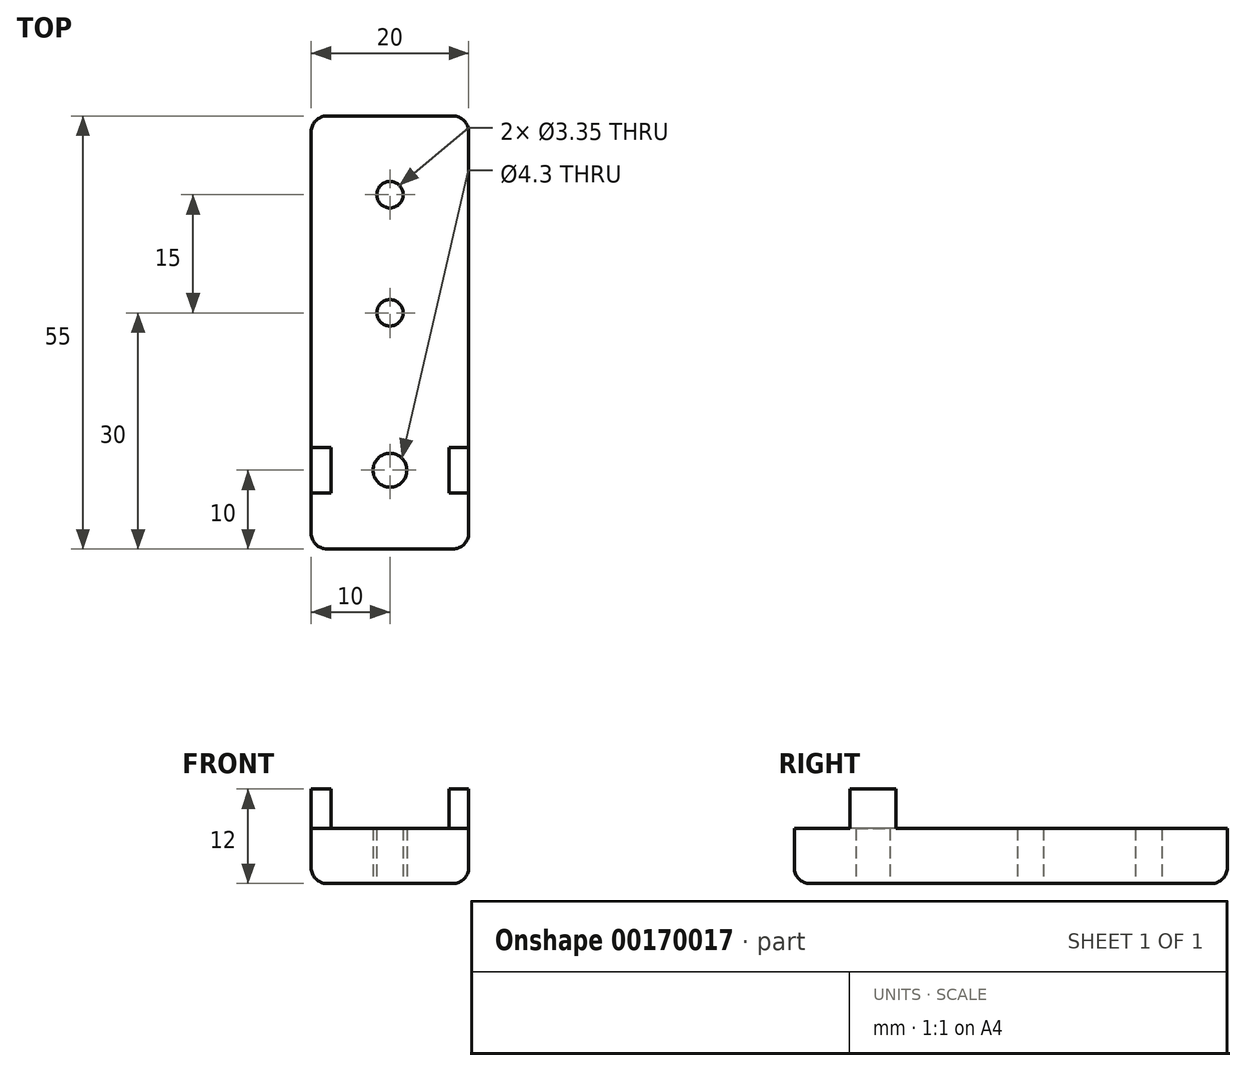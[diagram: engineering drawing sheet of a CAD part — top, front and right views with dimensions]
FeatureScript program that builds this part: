
annotation { "Feature Type Name" : "Feature", "Feature Type Description" : "" }
export const myFeature = defineFeature(function(context is Context, id is Id, definition is map)
    precondition{}
    {
        {
            var Q0;
            Q0=qCreatedBy(makeId("Top.planeOp"),FACE);
            var sketch = newSketch(context, id + "F0", { "sketchPlane" : qUnion([Q0])});
            skLineSegment(sketch, "E0.bottom", {"start": v(-10, 0) * mm, "end": v(10, 0) * mm});
            skLineSegment(sketch, "E0.top", {"start": v(-10, 55) * mm, "end": v(10, 55) * mm});
            skLineSegment(sketch, "E0.left", {"start": v(-10, 0) * mm, "end": v(-10, 55) * mm});
            skLineSegment(sketch, "E0.right", {"start": v(10, 0) * mm, "end": v(10, 55) * mm});
            skLineSegment(sketch, "E1.bottom", {"start": v(-7.5, 7.1) * mm, "end": v(-10, 7.1) * mm});
            skLineSegment(sketch, "E1.top", {"start": v(-7.5, 12.9) * mm, "end": v(-10, 12.9) * mm});
            skLineSegment(sketch, "E1.left", {"start": v(-7.5, 7.1) * mm, "end": v(-7.5, 12.9) * mm});
            skPoint(sketch, "E1.middle", {"position": v(-10, 10) * mm});
            skLineSegment(sketch, "E2.bottom", {"start": v(7.5, 12.9) * mm, "end": v(10, 12.9) * mm});
            skLineSegment(sketch, "E2.top", {"start": v(7.5, 7.1) * mm, "end": v(10, 7.1) * mm});
            skLineSegment(sketch, "E2.left", {"start": v(7.5, 12.9) * mm, "end": v(7.5, 7.1) * mm});
            skPoint(sketch, "E2.middle.positionSnap0", {"position": v(-7.5, 10) * mm});
            skPoint(sketch, "E2.centerSnap0", {"position": v(-7.5, 10) * mm});
            skCircle(sketch, "E3", {"center": v(0, 10) * mm, "radius": 2.15 * mm});
            skCircle(sketch, "E4", {"center": v(0, 45) * mm, "radius": 1.68 * mm});
            skPoint(sketch, "E4.centerSnap0", {"position": v(0, 55) * mm});
            skCircle(sketch, "E5", {"center": v(0, 30) * mm, "radius": 1.68 * mm});
            skSolve(sketch);
        }
        {
            var Q0;
            {var subQ5=sQuery(id+"F0.wireOp",EDGE,"E0.bottom");Q0=makeQuery(id+"F0.imprint","IMPRINT",FACE,{"disambiguationData":[TD([[makeQuery(id+"F0.imprint","IMPRINT",EDGE,{"derivedFrom":subQ5}),1.0]])]});}
            var Q1;
            {var subQ0=sQuery(id+"F0.wireOp",EDGE,"E1.bottom");Q1=makeQuery(id+"F0.imprint","IMPRINT",FACE,{"disambiguationData":[TD([[makeQuery(id+"F0.imprint","IMPRINT",EDGE,{"derivedFrom":subQ0}),-1.0]])]});}
            var Q2;
            {var subQ0=sQuery(id+"F0.wireOp",EDGE,"E2.bottom");Q2=makeQuery(id+"F0.imprint","IMPRINT",FACE,{"disambiguationData":[TD([[makeQuery(id+"F0.imprint","IMPRINT",EDGE,{"derivedFrom":subQ0}),-1.0]])]});}
            extrude(context, id + "F1", {"entities" : qUnion([Q0, Q1, Q2]), "depth" : 7 * mm});
        }
        {
            var Q0;
            {var subQ0=sQuery(id+"F0.wireOp",EDGE,"E1.bottom");Q0=makeQuery(id+"F0.imprint","IMPRINT",FACE,{"disambiguationData":[TD([[makeQuery(id+"F0.imprint","IMPRINT",EDGE,{"derivedFrom":subQ0}),-1.0]])]});}
            var Q1;
            {var subQ0=sQuery(id+"F0.wireOp",EDGE,"E2.bottom");Q1=makeQuery(id+"F0.imprint","IMPRINT",FACE,{"disambiguationData":[TD([[makeQuery(id+"F0.imprint","IMPRINT",EDGE,{"derivedFrom":subQ0}),-1.0]])]});}
            extrude(context, id + "F2", {"entities" : qUnion([Q0, Q1]), "operationType" : NewBodyOperationType.ADD, "depth" : (7 + 5) * mm});
        }
        {
            var Q0;
            Q0=makeQuery(id+"F1.opExtrude","SWEPT_EDGE",EDGE,{"disambiguationData":[OSD([sQuery(id+"F0.wireOp",EDGE,"E0.bottom"),sQuery(id+"F0.wireOp",EDGE,"E0.right")])]});
            var Q1;
            Q1=makeQuery(id+"F1.opExtrude","SWEPT_EDGE",EDGE,{"disambiguationData":[OSD([sQuery(id+"F0.wireOp",EDGE,"E0.bottom"),sQuery(id+"F0.wireOp",EDGE,"E0.left")])]});
            var Q2;
            Q2=makeQuery(id+"F1.opExtrude","SWEPT_EDGE",EDGE,{"disambiguationData":[OSD([sQuery(id+"F0.wireOp",EDGE,"E0.top"),sQuery(id+"F0.wireOp",EDGE,"E0.right")])]});
            var Q3;
            Q3=makeQuery(id+"F1.opExtrude","SWEPT_EDGE",EDGE,{"disambiguationData":[OSD([sQuery(id+"F0.wireOp",EDGE,"E0.top"),sQuery(id+"F0.wireOp",EDGE,"E0.left")])]});
            var Q4;
            Q4=makeQuery(id+"F1.opExtrude","CAP_EDGE",EDGE,{"disambiguationData":[OSD([sQuery(id+"F0.wireOp",EDGE,"E0.right")])],"isStart":true});
            var Q5;
            Q5=makeQuery(id+"F1.opExtrude","CAP_EDGE",EDGE,{"disambiguationData":[OSD([sQuery(id+"F0.wireOp",EDGE,"E0.bottom")])],"isStart":true});
            var Q6;
            Q6=makeQuery(id+"F1.opExtrude","CAP_EDGE",EDGE,{"disambiguationData":[OSD([sQuery(id+"F0.wireOp",EDGE,"E0.left")])],"isStart":true});
            var Q7;
            Q7=makeQuery(id+"F1.opExtrude","CAP_EDGE",EDGE,{"disambiguationData":[OSD([sQuery(id+"F0.wireOp",EDGE,"E0.top")])],"isStart":true});
            fillet(context, id + "F3", {"entities" : qUnion([Q0, Q1, Q2, Q3, Q4, Q5, Q6, Q7]), "radius" : 2 * mm, "tangentPropagation" : true, "allowEdgeOverflow" : false});
        }
    });
